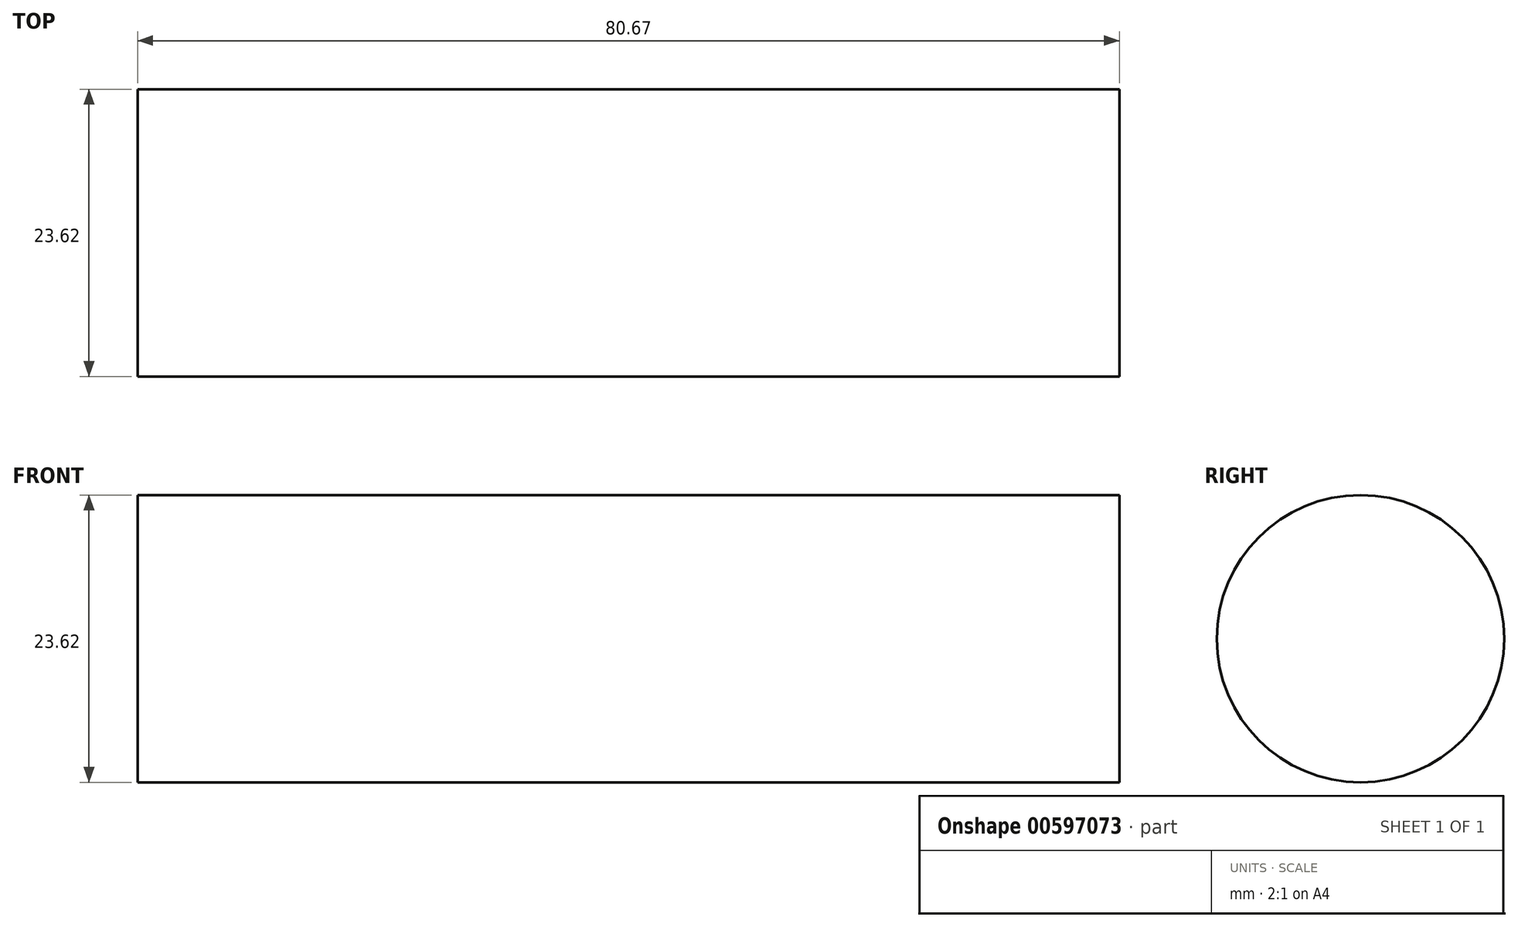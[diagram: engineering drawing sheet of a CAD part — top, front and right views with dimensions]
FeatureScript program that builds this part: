
annotation { "Feature Type Name" : "Feature", "Feature Type Description" : "" }
export const myFeature = defineFeature(function(context is Context, id is Id, definition is map)
    precondition{}
    {
        {
            var Q0;
            Q0=qCreatedBy(makeId("Right.planeOp"),FACE);
            var sketch = newSketch(context, id + "F0", { "sketchPlane" : qUnion([Q0])});
            skCircle(sketch, "E0", {"center": v(0, 0) * mm, "radius": 11.81 * mm});
            skSolve(sketch);
        }
        {
            var Q0;
            Q0 = qSketchRegion(id + "F0", true);
            extrude(context, id + "F1", {"entities" : qUnion([Q0]), "depth" : 80.67 * mm, "offsetDistance" : 25.4 * mm});
        }
    });
